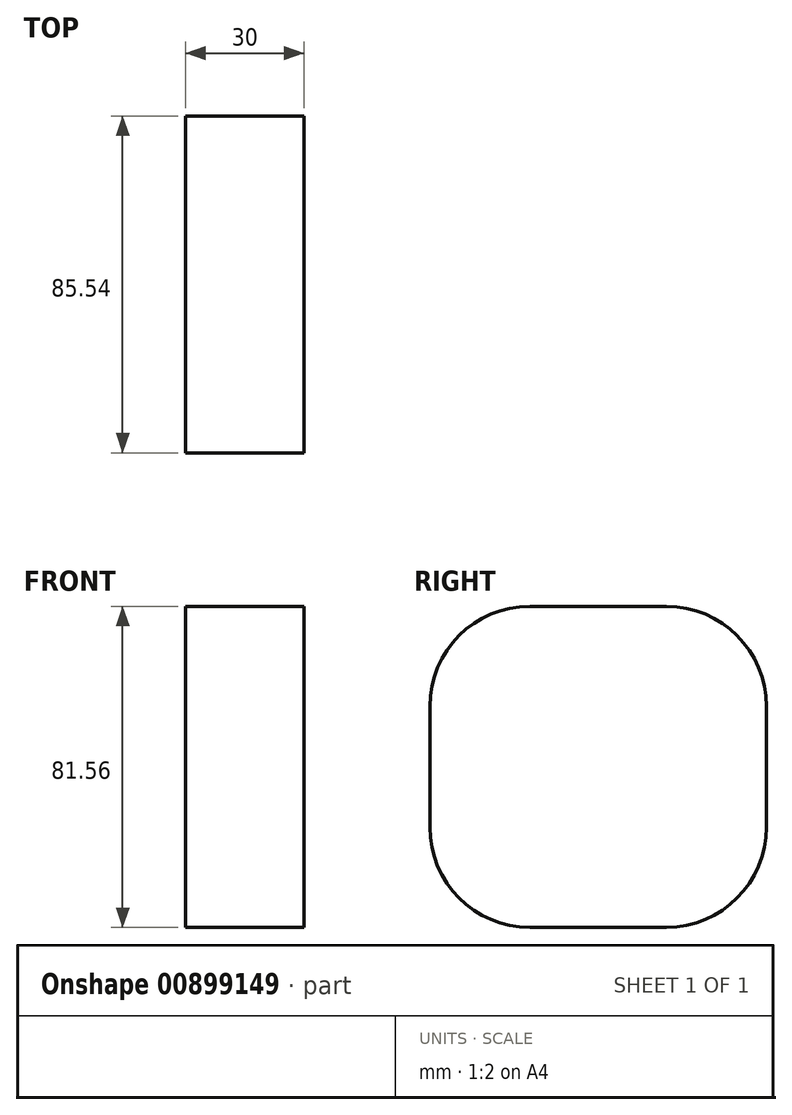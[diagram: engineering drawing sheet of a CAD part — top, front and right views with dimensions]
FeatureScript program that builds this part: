
annotation { "Feature Type Name" : "Feature", "Feature Type Description" : "" }
export const myFeature = defineFeature(function(context is Context, id is Id, definition is map)
    precondition{}
    {
        {
            var Q0;
            Q0=qCreatedBy(makeId("Right.planeOp"),FACE);
            var sketch = newSketch(context, id + "F0", { "sketchPlane" : qUnion([Q0])});
            skLineSegment(sketch, "E0.bottom", {"start": v(17.37, -40.78) * mm, "end": v(-17.37, -40.78) * mm});
            skLineSegment(sketch, "E0.top", {"start": v(17.37, 40.78) * mm, "end": v(-17.37, 40.78) * mm});
            skLineSegment(sketch, "E0.left", {"start": v(42.77, -15.38) * mm, "end": v(42.77, 15.38) * mm});
            skLineSegment(sketch, "E0.right", {"start": v(-42.77, -15.38) * mm, "end": v(-42.77, 15.38) * mm});
            skPoint(sketch, "E0.middle", {"position": v(0, 0) * mm});
            skPoint(sketch, "E1.visualSharp", {"position": v(42.77, 40.78) * mm});
            skArc(sketch, "E1.filletArc", {"start": v(42.77, 15.38) * mm, "mid": v(35.33, 33.34) * mm, "end": v(17.37, 40.78) * mm});
            skPoint(sketch, "E2.visualSharp", {"position": v(-42.77, 40.78) * mm});
            skArc(sketch, "E2.filletArc", {"start": v(-17.37, 40.78) * mm, "mid": v(-35.33, 33.34) * mm, "end": v(-42.77, 15.38) * mm});
            skPoint(sketch, "E3.visualSharp", {"position": v(42.77, -40.78) * mm});
            skArc(sketch, "E3.filletArc", {"start": v(17.37, -40.78) * mm, "mid": v(35.33, -33.34) * mm, "end": v(42.77, -15.38) * mm});
            skPoint(sketch, "E4.visualSharp", {"position": v(-42.77, -40.78) * mm});
            skArc(sketch, "E4.filletArc", {"start": v(-42.77, -15.38) * mm, "mid": v(-35.33, -33.34) * mm, "end": v(-17.37, -40.78) * mm});
            skSolve(sketch);
        }
        {
            var Q0;
            Q0=makeQuery(id+"F0.imprint","IMPRINT",FACE,{"disambiguationData":[TD([[makeQuery(id+"F0.imprint","IMPRINT",EDGE,{"derivedFrom":sQuery(id+"F0.wireOp",EDGE,"E0.bottom")}),-1.0]])]});
            extrude(context, id + "F1", {"entities" : qUnion([Q0]), "depth" : 30 * mm, "offsetDistance" : 25.4 * mm});
        }
    });
